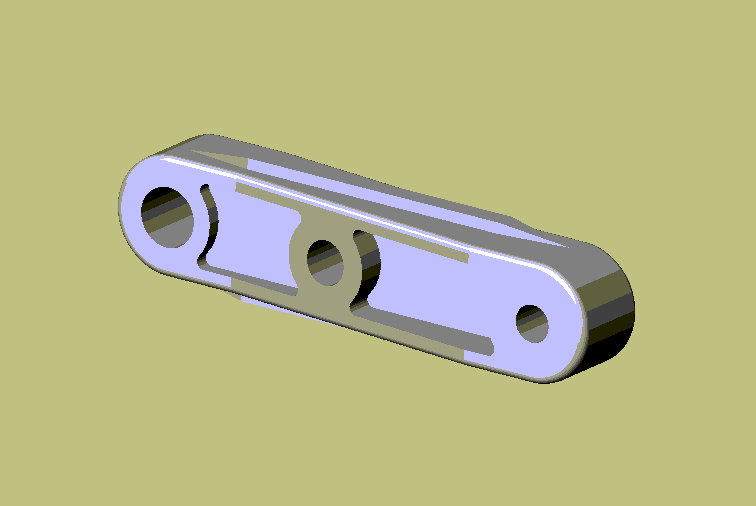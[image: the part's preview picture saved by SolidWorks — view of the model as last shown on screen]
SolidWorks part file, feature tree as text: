
SOLIDWORKS PART (.sldprt)
format: sldprt  version: not decoded by parser v0  size: 273,408 bytes
history: native  units: mm
features: sketch x7, plane x4, cut_extrude x4, extrude x3, fillet x2, material x1, mirror x1 (+8 scaffold rows collapsed)
feature tree (30):
  scaffold x8  (default folders/planes/origin — collapsed)
  material  "Matériau <non spécifié>"
  plane  "Plane1"
  plane  "Plane2"
  plane  "Plane3"
  sketch  "Esquisse1"  dims[D2=8.0mm D3=8.0mm D4=4.0mm D5=3.0mm D1=29.0mm D6=12.5mm]
  extrude  "Base-Extrusion"  Depth=8mm
  sketch  "Esquisse2"  dims[c1.D1=9.0mm c1.D2=19.0mm c1.D3=9.0mm c1.D4=6.0mm c1.D5=6.0mm c1.D6=19.0mm c2.D3=5.0mm]
  cut_extrude  "Enlèv. mat.-Extru.1"  Depth=48mm
  sketch  "Esquisse3"  dims[D1=6.0mm D2=7.0mm D3=0.5mm]
  cut_extrude  "Enlèv. mat.-Extru.2"  Depth=3mm
  plane  "Plan1"  Offset=4mm
  mirror  "Symétrie1"
  sketch  "Esquisse7"  dims[D1=4.0mm D2=1.5mm D3=19.0mm D4=5.0mm D5=5.0mm]
  extrude  "Boss.-Extru.2"  Depth=0.75mm
  extrude  "Symétrie2"  [1 undecoded]
  sketch  "Esquisse8"
  cut_extrude  "Enlèv. mat.-Extru.3"  [1 undecoded]
  fillet  "Congé1"  Radius=0.5mm
  sketch  "Esquisse9"  dims[D1=6.0mm]
  fillet  "Boss.-Extru.3"  Radius=1mm
  sketch  "Esquisse10"  dims[D1=2.5mm]
  cut_extrude  "Enlèv. mat.-Extru.4"  [1 undecoded]
decode coverage: 12 of 17 modeling features carry decoded parameters
note: 3 parameter values undecoded
summary: no parameter record found for 3 features
note: suppression state not decoded; provenance and decode notes live in map.json
